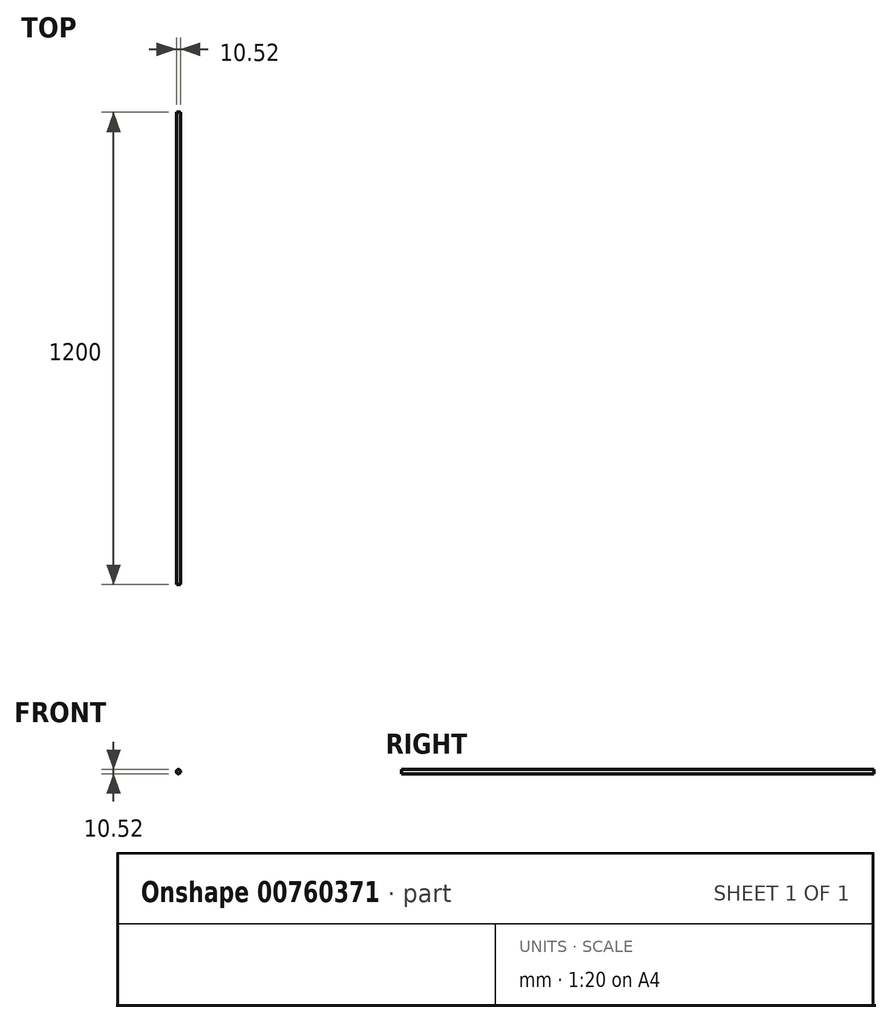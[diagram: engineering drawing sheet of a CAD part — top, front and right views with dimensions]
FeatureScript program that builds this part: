
annotation { "Feature Type Name" : "Feature", "Feature Type Description" : "" }
export const myFeature = defineFeature(function(context is Context, id is Id, definition is map)
    precondition{}
    {
        {
            assignVariable(context, id + "F0", {"name" : "LENGTH", "anyValue" : 1200});
        }
        {
            var Q0;
            Q0=qCreatedBy(makeId("Front.planeOp"),FACE);
            var sketch = newSketch(context, id + "F1", { "sketchPlane" : qUnion([Q0])});
            skCircle(sketch, "E0", {"center": v(0, 0) * mm, "radius": 5.26 * mm});
            skSolve(sketch);
        }
        {
            var Q0;
            Q0=makeQuery(id+"F1.imprint","IMPRINT",FACE,{"disambiguationData":[TD([[makeQuery(id+"F1.imprint","IMPRINT",EDGE,{"derivedFrom":sQuery(id+"F1.wireOp",EDGE,"E0")}),1.0]])]});
            extrude(context, id + "F2", {"entities" : qUnion([Q0]), "oppositeDirection" : true, "depth" : (getVariable(context, 'LENGTH')) * mm, "offsetDistance" : 25 * mm});
        }
    });
